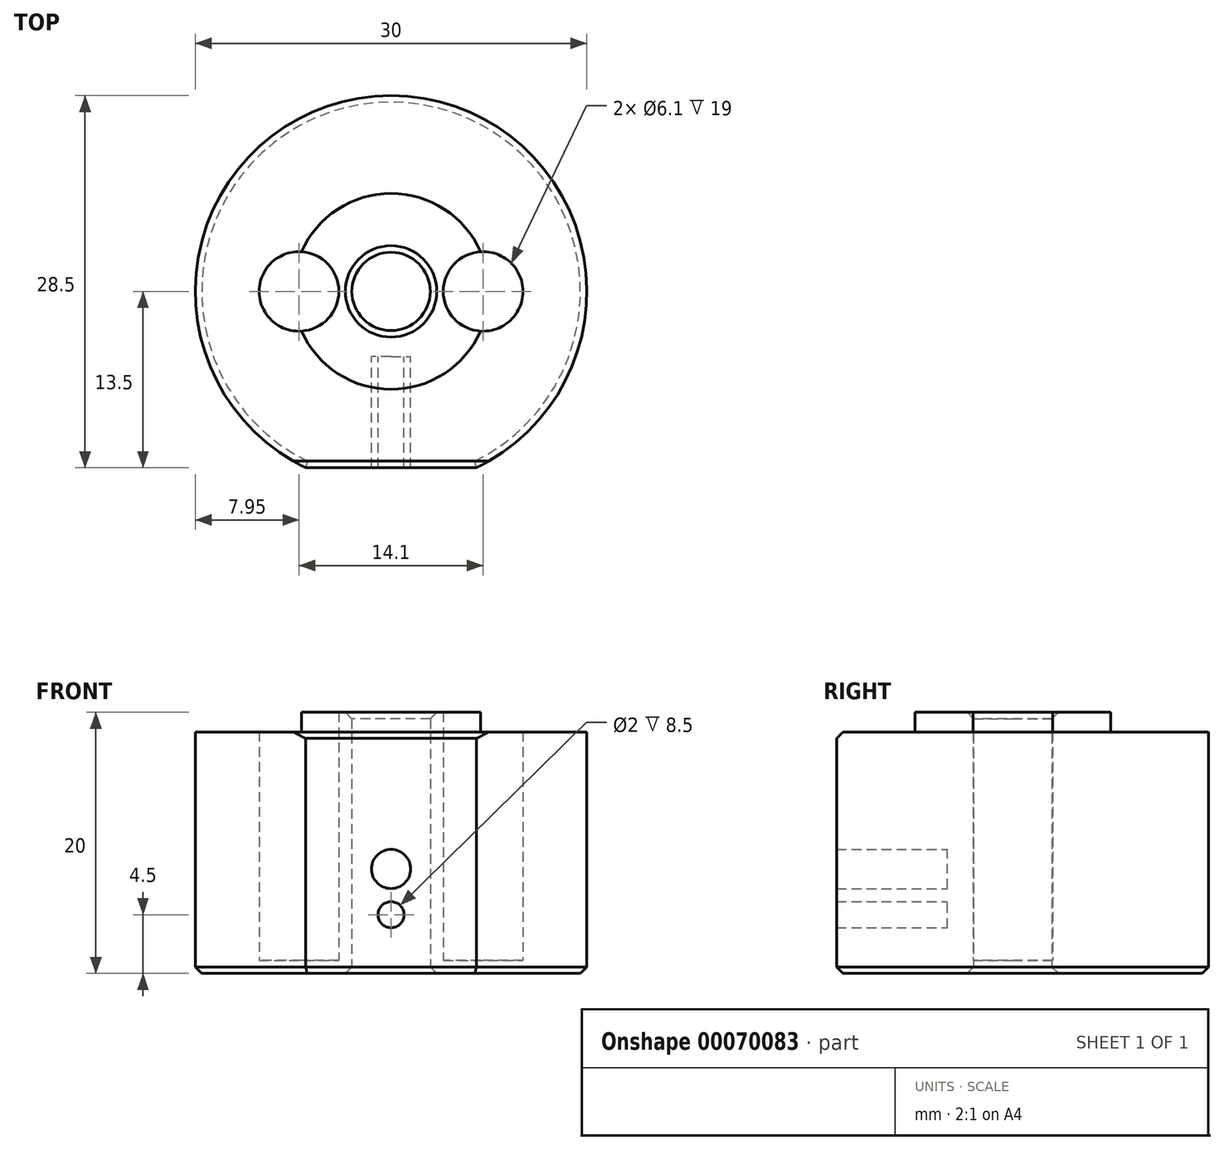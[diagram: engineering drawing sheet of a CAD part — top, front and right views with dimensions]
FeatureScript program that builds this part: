
annotation { "Feature Type Name" : "Feature", "Feature Type Description" : "" }
export const myFeature = defineFeature(function(context is Context, id is Id, definition is map)
    precondition{}
    {
        {
            var Q0;
            Q0=qCreatedBy(makeId("Top.planeOp"),FACE);
            var sketch = newSketch(context, id + "F0", { "sketchPlane" : qUnion([Q0])});
            skCircle(sketch, "E0", {"center": v(0, 0) * mm, "radius": 15 * mm});
            skCircle(sketch, "E1", {"center": v(0, 0) * mm, "radius": 3 * mm});
            skCircle(sketch, "E2", {"center": v(-7.05, 0) * mm, "radius": 3.05 * mm});
            skCircle(sketch, "E3", {"center": v(7.05, 0) * mm, "radius": 3.05 * mm});
            skSolve(sketch);
        }
        {
            var Q0;
            Q0=makeQuery(id+"F0.imprint","IMPRINT",FACE,{"disambiguationData":[TD([[makeQuery(id+"F0.imprint","IMPRINT",EDGE,{"derivedFrom":sQuery(id+"F0.wireOp",EDGE,"E0")}),1.0]])]});
            extrude(context, id + "F1", {"entities" : qUnion([Q0]), "depth" : 20 * mm});
        }
        {
            var Q0;
            Q0=makeQuery(id+"F0.imprint","IMPRINT",FACE,{"disambiguationData":[TD([[makeQuery(id+"F0.imprint","IMPRINT",EDGE,{"derivedFrom":sQuery(id+"F0.wireOp",EDGE,"E2")}),1.0]])]});
            var Q1;
            Q1=makeQuery(id+"F0.imprint","IMPRINT",FACE,{"disambiguationData":[TD([[makeQuery(id+"F0.imprint","IMPRINT",EDGE,{"derivedFrom":sQuery(id+"F0.wireOp",EDGE,"E3")}),1.0]])]});
            extrude(context, id + "F2", {"entities" : qUnion([Q0, Q1]), "operationType" : NewBodyOperationType.ADD, "depth" : 1 * mm});
        }
        {
            var Q0;
            Q0=makeQuery(id+"F1.opExtrude","CAP_FACE",FACE,{"disambiguationData":[OSD([sQuery(id+"F0.wireOp",EDGE,"E0"),sQuery(id+"F0.wireOp",EDGE,"E1"),sQuery(id+"F0.wireOp",EDGE,"E2"),sQuery(id+"F0.wireOp",EDGE,"E3")])],"isStart":false});
            var sketch = newSketch(context, id + "F3", { "sketchPlane" : qUnion([Q0])});
            skCircle(sketch, "E4", {"center": v(0, 0) * mm, "radius": 7.5 * mm});
            skSolve(sketch);
        }
        {
            var Q0;
            Q0=makeQuery(id+"F3.imprint","IMPRINT",FACE,{"disambiguationData":[TD([[makeQuery(id+"F3.imprint","IMPRINT",EDGE,{"derivedFrom":makeQuery(id+"F1.opExtrude","CAP_EDGE",EDGE,{"disambiguationData":[OSD([sQuery(id+"F0.wireOp",EDGE,"E0")])],"isStart":false})}),1.0]])]});
            extrude(context, id + "F4", {"entities" : qUnion([Q0]), "operationType" : NewBodyOperationType.REMOVE, "oppositeDirection" : true, "depth" : 1.5 * mm});
        }
        {
            var Q0;
            Q0=qCreatedBy(makeId("Front.planeOp"),FACE);
            var sketch = newSketch(context, id + "F5", { "sketchPlane" : qUnion([Q0])});
            skCircle(sketch, "E5", {"center": v(0, 4.5) * mm, "radius": 1 * mm});
            skCircle(sketch, "E6", {"center": v(0, 8) * mm, "radius": 1.5 * mm});
            skSolve(sketch);
        }
        {
            var Q0;
            Q0 = qSketchRegion(id + "F5", true);
            extrude(context, id + "F6", {"entities" : qUnion([Q0]), "operationType" : NewBodyOperationType.REMOVE, "depth" : 25 * mm, "hasSecondDirection" : true, "secondDirectionOppositeDirection" : false, "secondDirectionDepth" : 5 * mm});
        }
        {
            var Q0;
            Q0=makeQuery(id+"F0.imprint","IMPRINT",FACE,{"disambiguationData":[TD([[makeQuery(id+"F0.imprint","IMPRINT",EDGE,{"derivedFrom":sQuery(id+"F0.wireOp",EDGE,"E0")}),1.0]])]});
            var sketch = newSketch(context, id + "F7", { "sketchPlane" : qUnion([Q0])});
            skLineSegment(sketch, "E7", {"start": v(-6.54, -13.5) * mm, "end": v(6.54, -13.5) * mm});
            skCircle(sketch, "E8.0", {"center": v(0, 0) * mm, "radius": 15 * mm});
            skSolve(sketch);
        }
        {
            var Q0;
            {var subQ0=sQuery(id+"F7.wireOp",EDGE,"E7");Q0=makeQuery(id+"F7.imprint","IMPRINT",FACE,{"disambiguationData":[TD([[makeQuery(id+"F7.imprint","IMPRINT",EDGE,{"derivedFrom":subQ0}),-1.0]])]});}
            extrude(context, id + "F8", {"entities" : qUnion([Q0]), "operationType" : NewBodyOperationType.REMOVE, "depth" : 25 * mm});
        }
        {
            var Q0;
            {var subQ0=sQuery(id+"F0.wireOp",EDGE,"E3");var subQ1=sQuery(id+"F0.wireOp",EDGE,"E2");Q0=makeQuery(id+"F2.boolean.opBoolean","MERGE",FACE,{"derivedFrom":[makeQuery(id+"F1.opExtrude","CAP_FACE",FACE,{"disambiguationData":[OSD([sQuery(id+"F0.wireOp",EDGE,"E0"),sQuery(id+"F0.wireOp",EDGE,"E1"),subQ1,subQ0])],"isStart":true}),makeQuery(id+"F2.opExtrude","CAP_FACE",FACE,{"disambiguationData":[OSD([subQ1])],"isStart":true}),makeQuery(id+"F2.opExtrude","CAP_FACE",FACE,{"disambiguationData":[OSD([subQ0])],"isStart":true})]});}
            var Q1;
            Q1=makeQuery(id+"F4.boolean.opBoolean","COPY",EDGE,{"derivedFrom":makeQuery(id+"F4.opExtrude","CAP_EDGE",EDGE,{"disambiguationData":[OSD([sQuery(id+"F0.wireOp",EDGE,"E0")])],"isStart":false})});
            var Q2;
            Q2=makeQuery(id+"F1.opExtrude","CAP_EDGE",EDGE,{"disambiguationData":[OSD([sQuery(id+"F0.wireOp",EDGE,"E1")])],"isStart":false});
            var Q3;
            Q3=makeQuery(id+"F8.boolean.opBoolean","INTERSECT",EDGE,{"derivedFrom":[makeQuery(id+"F4.boolean.opBoolean","COPY",FACE,{"derivedFrom":makeQuery(id+"F4.opExtrude","CAP_FACE",FACE,{"disambiguationData":[OSD([sQuery(id+"F0.wireOp",EDGE,"E0"),sQuery(id+"F0.wireOp",EDGE,"E2"),sQuery(id+"F0.wireOp",EDGE,"E3"),sQuery(id+"F3.wireOp",EDGE,"E4")])],"isStart":false})}),makeQuery(id+"F8.opExtrude","SWEPT_FACE",FACE,{"disambiguationData":[OSD([sQuery(id+"F7.wireOp",EDGE,"E7")])]})]});
            chamfer(context, id + "F9", {"entities" : qUnion([Q0, Q1, Q2, Q3]), "width" : 0.5 * mm, "tangentPropagation" : true});
        }
    });
